# Revit family: M-1001-DX
name_source: partatom
category: Plumbing Fixtures
revit_build: Autodesk Revit 2016 (Build: 20150714_1515(x64)
units: mm (PartAtom-declared; Revit-internal decimal feet)

## family parameters
Always vertical = Yes
Cut with Voids When Loaded = No
OmniClass Number = 23.45.00.00
OmniClass Title = Sanitary, Laundry, and Cleaning Equipment
Part Type = Normal
Room Calculation Point = No
Round Connector Dimension = Use Diameter
Shared = Yes
Work Plane-Based = Yes

## types (1)
- M-1001-DX
    Accessories = Desagüe de Push con rebosadreo, inserto para Rebosadero, herramienta para sujeción, llave para Aireador, llave Allen 5/64"
    Default Elevation = 35.0"
    Description = Mezcladora para Lavabo con Desagüe de Push
    Gasto Maximo = 0.0 GPM
    Manufacturer = Helvex S.A. de C.V.
    Materials = Cuerpo de lat魛伖n
    Model = M-1001-DX
    Presión Máxima de Trabajo = 14.2 psi
    Presión Mínima de Trabajo = 85.3 psi
    Product Features = Ensamble de 8", 10" o 12" con desagüe de push y valvex a nivel izquierdo y derecho de discos cerámicos a 1/4 de vuelta, con manerales.
    Type Comments = Mezcladora Vertica M-1001-DX con Desagüe de Push
    URL = http://www.helvex.com.mx
    Valves = Valvex derecho, Valvex izquierdo

## geometry (parser evidence)
native form markers: Sweep x3
no freeform markers — native parametric forms only
